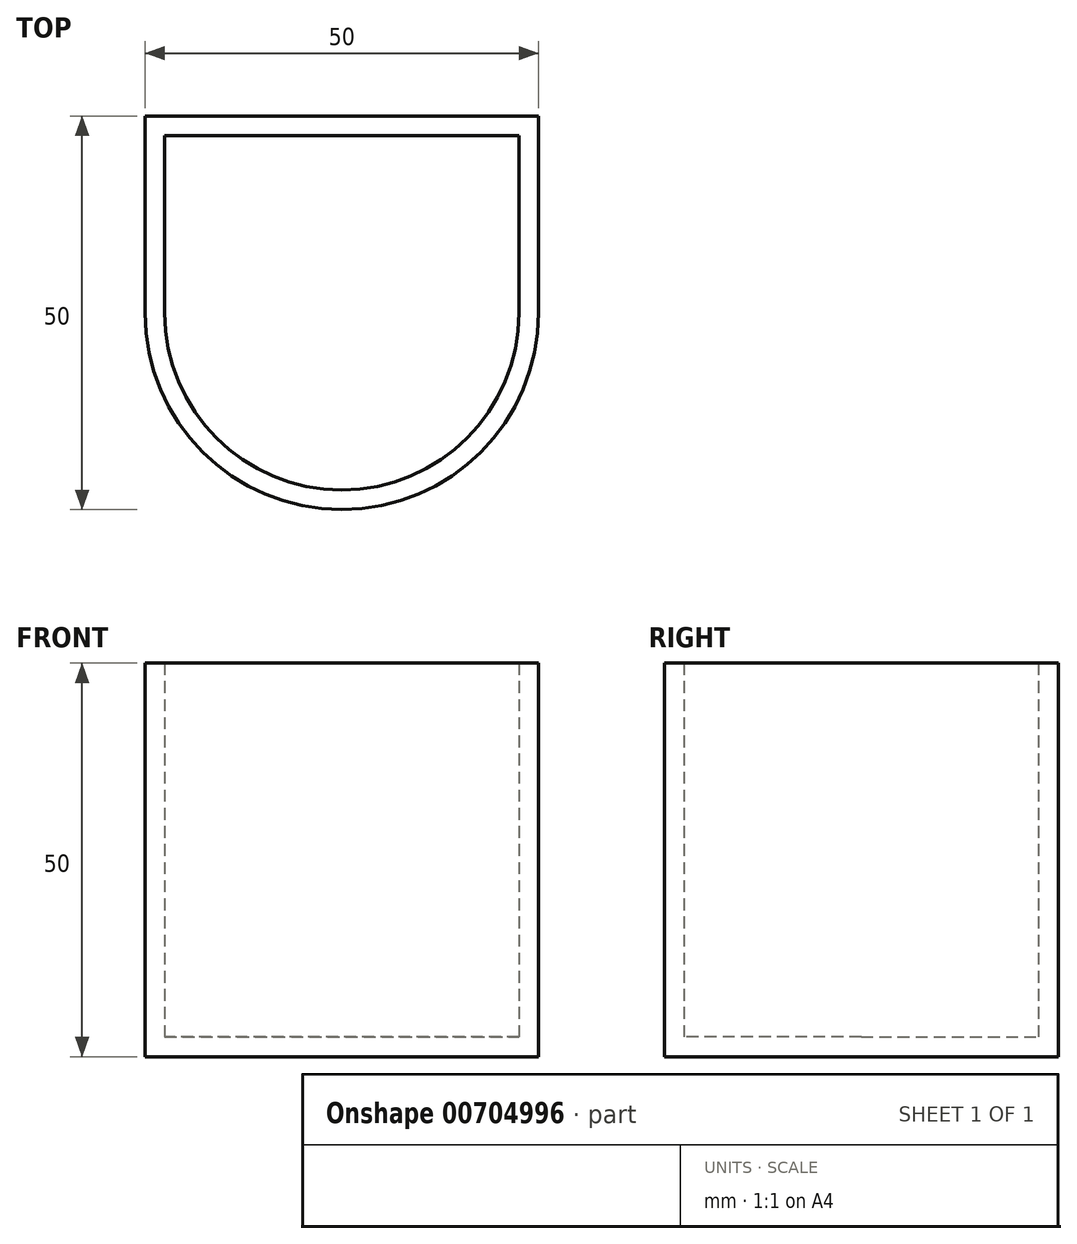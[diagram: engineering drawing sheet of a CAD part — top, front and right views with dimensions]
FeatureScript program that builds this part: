
annotation { "Feature Type Name" : "Feature", "Feature Type Description" : "" }
export const myFeature = defineFeature(function(context is Context, id is Id, definition is map)
    precondition{}
    {
        {
            var Q0;
            Q0=qCreatedBy(makeId("Top.planeOp"),FACE);
            var sketch = newSketch(context, id + "F0", { "sketchPlane" : qUnion([Q0])});
            skLineSegment(sketch, "E0.bottom", {"start": v(25, -25) * mm, "end": v(-25, -25) * mm});
            skLineSegment(sketch, "E0.top", {"start": v(25, 25) * mm, "end": v(-25, 25) * mm});
            skLineSegment(sketch, "E0.left", {"start": v(25, -25) * mm, "end": v(25, 25) * mm});
            skLineSegment(sketch, "E0.right", {"start": v(-25, -25) * mm, "end": v(-25, 25) * mm});
            skPoint(sketch, "E0.middle", {"position": v(0, 0) * mm});
            skSolve(sketch);
        }
        {
            var Q0;
            Q0=makeQuery(id+"F0.imprint","IMPRINT",FACE,{"disambiguationData":[TD([[makeQuery(id+"F0.imprint","IMPRINT",EDGE,{"derivedFrom":sQuery(id+"F0.wireOp",EDGE,"E0.bottom")}),-1.0]])]});
            extrude(context, id + "F1", {"entities" : qUnion([Q0]), "depth" : 50 * mm, "offsetDistance" : 25 * mm});
        }
        {
            var Q0;
            Q0=makeQuery(id+"F1.opExtrude","SWEPT_EDGE",EDGE,{"disambiguationData":[OSD([sQuery(id+"F0.wireOp",EDGE,"E0.bottom"),sQuery(id+"F0.wireOp",EDGE,"E0.left")])]});
            var Q1;
            Q1=makeQuery(id+"F1.opExtrude","SWEPT_EDGE",EDGE,{"disambiguationData":[OSD([sQuery(id+"F0.wireOp",EDGE,"E0.bottom"),sQuery(id+"F0.wireOp",EDGE,"E0.right")])]});
            fillet(context, id + "F2", {"entities" : qUnion([Q0, Q1]), "radius" : 25 * mm, "tangentPropagation" : true, "allowEdgeOverflow" : false});
        }
        {
            var Q0;
            Q0=makeQuery(id+"F1.opExtrude","CAP_FACE",FACE,{"disambiguationData":[OSD([sQuery(id+"F0.wireOp",EDGE,"E0.bottom"),sQuery(id+"F0.wireOp",EDGE,"E0.top"),sQuery(id+"F0.wireOp",EDGE,"E0.left"),sQuery(id+"F0.wireOp",EDGE,"E0.right")])],"isStart":false});
            shell(context, id + "F3", {"entities" : qUnion([Q0]), "thickness" : 2.5 * mm});
        }
    });
